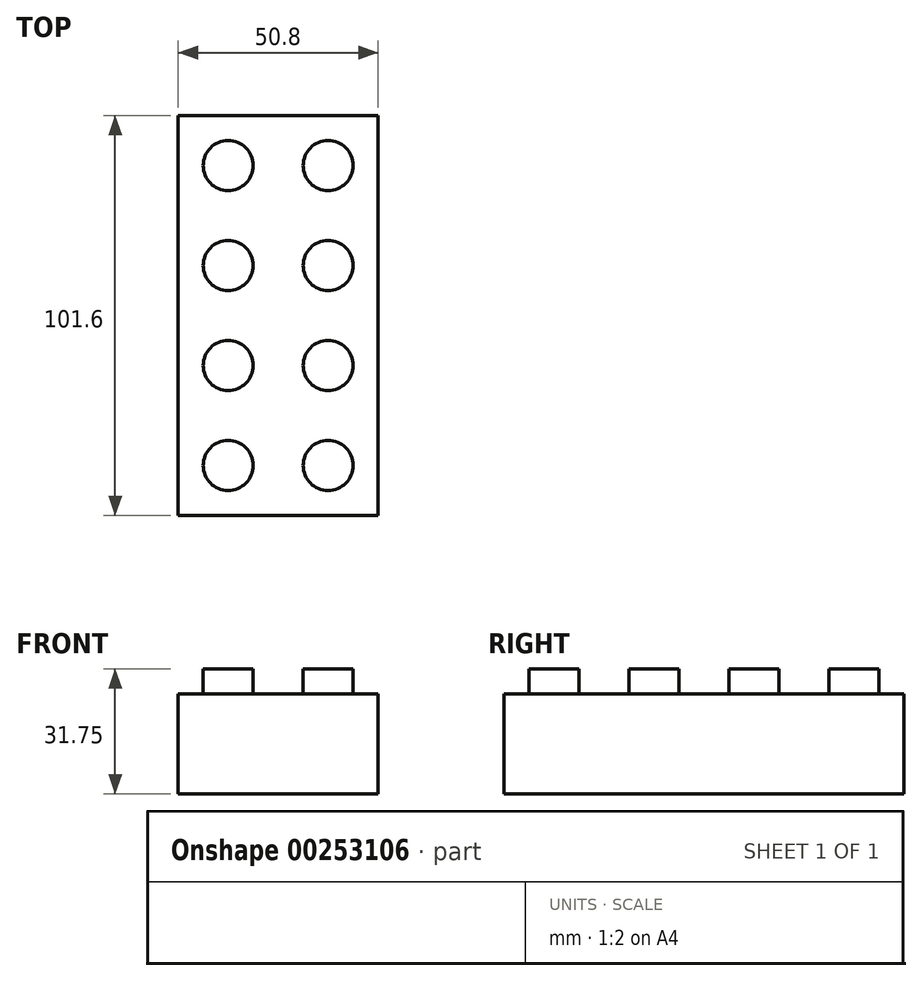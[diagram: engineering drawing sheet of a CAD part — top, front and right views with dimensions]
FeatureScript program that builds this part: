
annotation { "Feature Type Name" : "Feature", "Feature Type Description" : "" }
export const myFeature = defineFeature(function(context is Context, id is Id, definition is map)
    precondition{}
    {
        {
            var Q0;
            Q0=qCreatedBy(makeId("Top.planeOp"),FACE);
            var sketch = newSketch(context, id + "F0", { "sketchPlane" : qUnion([Q0])});
            skLineSegment(sketch, "E0.bottom", {"start": v(-21.4, 47.5) * mm, "end": v(29.4, 47.5) * mm});
            skLineSegment(sketch, "E0.top", {"start": v(-21.4, -54.1) * mm, "end": v(29.4, -54.1) * mm});
            skLineSegment(sketch, "E0.left", {"start": v(-21.4, 47.5) * mm, "end": v(-21.4, -54.1) * mm});
            skLineSegment(sketch, "E0.right", {"start": v(29.4, 47.5) * mm, "end": v(29.4, -54.1) * mm});
            skLineSegment(sketch, "E1", {"start": v(-21.4, 47.5) * mm, "end": v(-8.7, 47.5) * mm});
            skLineSegment(sketch, "E2", {"start": v(-8.7, 47.5) * mm, "end": v(29.4, 47.5) * mm});
            skLineSegment(sketch, "E3", {"start": v(16.7, 47.5) * mm, "end": v(29.4, 47.5) * mm});
            skLineSegment(sketch, "E4", {"start": v(-21.4, 47.5) * mm, "end": v(-21.4, 34.8) * mm});
            skLineSegment(sketch, "E5", {"start": v(-21.4, -54.1) * mm, "end": v(-21.4, -41.4) * mm});
            skCircle(sketch, "E6", {"center": v(-8.7, 34.8) * mm, "radius": 6.35 * mm});
            skCircle(sketch, "E7", {"center": v(16.7, 34.8) * mm, "radius": 6.35 * mm});
            skCircle(sketch, "E8", {"center": v(-8.7, -41.4) * mm, "radius": 6.35 * mm});
            skCircle(sketch, "E9", {"center": v(16.7, -41.4) * mm, "radius": 6.35 * mm});
            skLineSegment(sketch, "E10", {"start": v(-21.4, 34.8) * mm, "end": v(-21.4, 9.4) * mm});
            skLineSegment(sketch, "E11", {"start": v(-21.4, 9.4) * mm, "end": v(-21.4, -16) * mm});
            skCircle(sketch, "E12", {"center": v(-8.7, 9.4) * mm, "radius": 6.35 * mm});
            skCircle(sketch, "E13", {"center": v(16.7, 9.4) * mm, "radius": 6.35 * mm});
            skCircle(sketch, "E14", {"center": v(16.7, -16) * mm, "radius": 6.35 * mm});
            skCircle(sketch, "E15", {"center": v(-8.7, -16) * mm, "radius": 6.35 * mm});
            skSolve(sketch);
        }
        {
            var Q0;
            Q0 = qSketchRegion(id + "F0", true);
            extrude(context, id + "F1", {"entities" : qUnion([Q0]), "depth" : 25.4 * mm});
        }
        {
            var Q0;
            Q0=makeQuery(id+"F0.imprint","IMPRINT",FACE,{"disambiguationData":[TD([[makeQuery(id+"F0.imprint","IMPRINT",EDGE,{"derivedFrom":sQuery(id+"F0.wireOp",EDGE,"E6")}),1.0]])]});
            var Q1;
            Q1=makeQuery(id+"F0.imprint","IMPRINT",FACE,{"disambiguationData":[TD([[makeQuery(id+"F0.imprint","IMPRINT",EDGE,{"derivedFrom":sQuery(id+"F0.wireOp",EDGE,"E7")}),1.0]])]});
            var Q2;
            Q2=makeQuery(id+"F0.imprint","IMPRINT",FACE,{"disambiguationData":[TD([[makeQuery(id+"F0.imprint","IMPRINT",EDGE,{"derivedFrom":sQuery(id+"F0.wireOp",EDGE,"E13")}),1.0]])]});
            var Q3;
            Q3=makeQuery(id+"F0.imprint","IMPRINT",FACE,{"disambiguationData":[TD([[makeQuery(id+"F0.imprint","IMPRINT",EDGE,{"derivedFrom":sQuery(id+"F0.wireOp",EDGE,"E12")}),1.0]])]});
            var Q4;
            Q4=makeQuery(id+"F0.imprint","IMPRINT",FACE,{"disambiguationData":[TD([[makeQuery(id+"F0.imprint","IMPRINT",EDGE,{"derivedFrom":sQuery(id+"F0.wireOp",EDGE,"E15")}),1.0]])]});
            var Q5;
            Q5=makeQuery(id+"F0.imprint","IMPRINT",FACE,{"disambiguationData":[TD([[makeQuery(id+"F0.imprint","IMPRINT",EDGE,{"derivedFrom":sQuery(id+"F0.wireOp",EDGE,"E14")}),1.0]])]});
            var Q6;
            Q6=makeQuery(id+"F0.imprint","IMPRINT",FACE,{"disambiguationData":[TD([[makeQuery(id+"F0.imprint","IMPRINT",EDGE,{"derivedFrom":sQuery(id+"F0.wireOp",EDGE,"E8")}),1.0]])]});
            var Q7;
            Q7=makeQuery(id+"F0.imprint","IMPRINT",FACE,{"disambiguationData":[TD([[makeQuery(id+"F0.imprint","IMPRINT",EDGE,{"derivedFrom":sQuery(id+"F0.wireOp",EDGE,"E9")}),1.0]])]});
            extrude(context, id + "F2", {"entities" : qUnion([Q0, Q1, Q2, Q3, Q4, Q5, Q6, Q7]), "operationType" : NewBodyOperationType.ADD, "depth" : 31.75 * mm});
        }
    });
